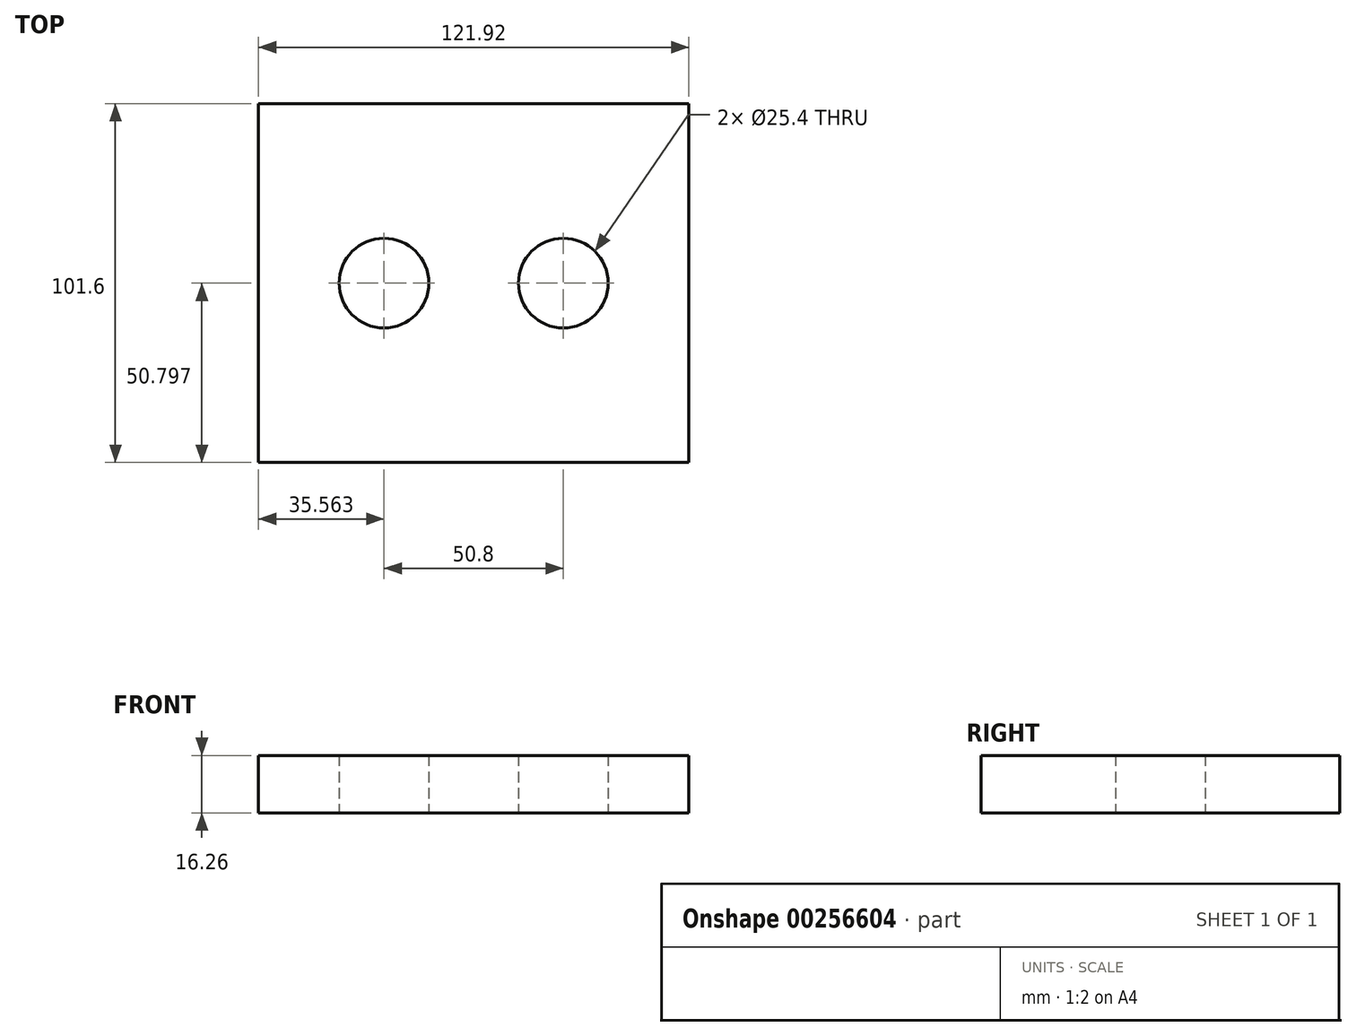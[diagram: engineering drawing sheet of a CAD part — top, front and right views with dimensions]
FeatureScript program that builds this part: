
annotation { "Feature Type Name" : "Feature", "Feature Type Description" : "" }
export const myFeature = defineFeature(function(context is Context, id is Id, definition is map)
    precondition{}
    {
        {
            var Q0;
            Q0=qCreatedBy(makeId("Top.planeOp"),FACE);
            var sketch = newSketch(context, id + "F0", { "sketchPlane" : qUnion([Q0])});
            skLineSegment(sketch, "E0.bottom", {"start": v(-63.12, 69.1) * mm, "end": v(58.8, 69.1) * mm});
            skLineSegment(sketch, "E0.top", {"start": v(-63.12, -32.5) * mm, "end": v(58.8, -32.5) * mm});
            skLineSegment(sketch, "E0.left", {"start": v(-63.12, 69.1) * mm, "end": v(-63.12, -32.5) * mm});
            skLineSegment(sketch, "E0.right", {"start": v(58.8, 69.1) * mm, "end": v(58.8, -32.5) * mm});
            skCircle(sketch, "E1", {"center": v(-27.56, 18.3) * mm, "radius": 12.7 * mm});
            skCircle(sketch, "E2", {"center": v(23.24, 18.3) * mm, "radius": 12.7 * mm});
            skSolve(sketch);
        }
        {
            var Q0;
            Q0=qSketchRegion(id+"F0",true);
            extrude(context, id + "F1", {"entities" : qUnion([Q0]), "depth" : 16.26 * mm});
        }
    });
